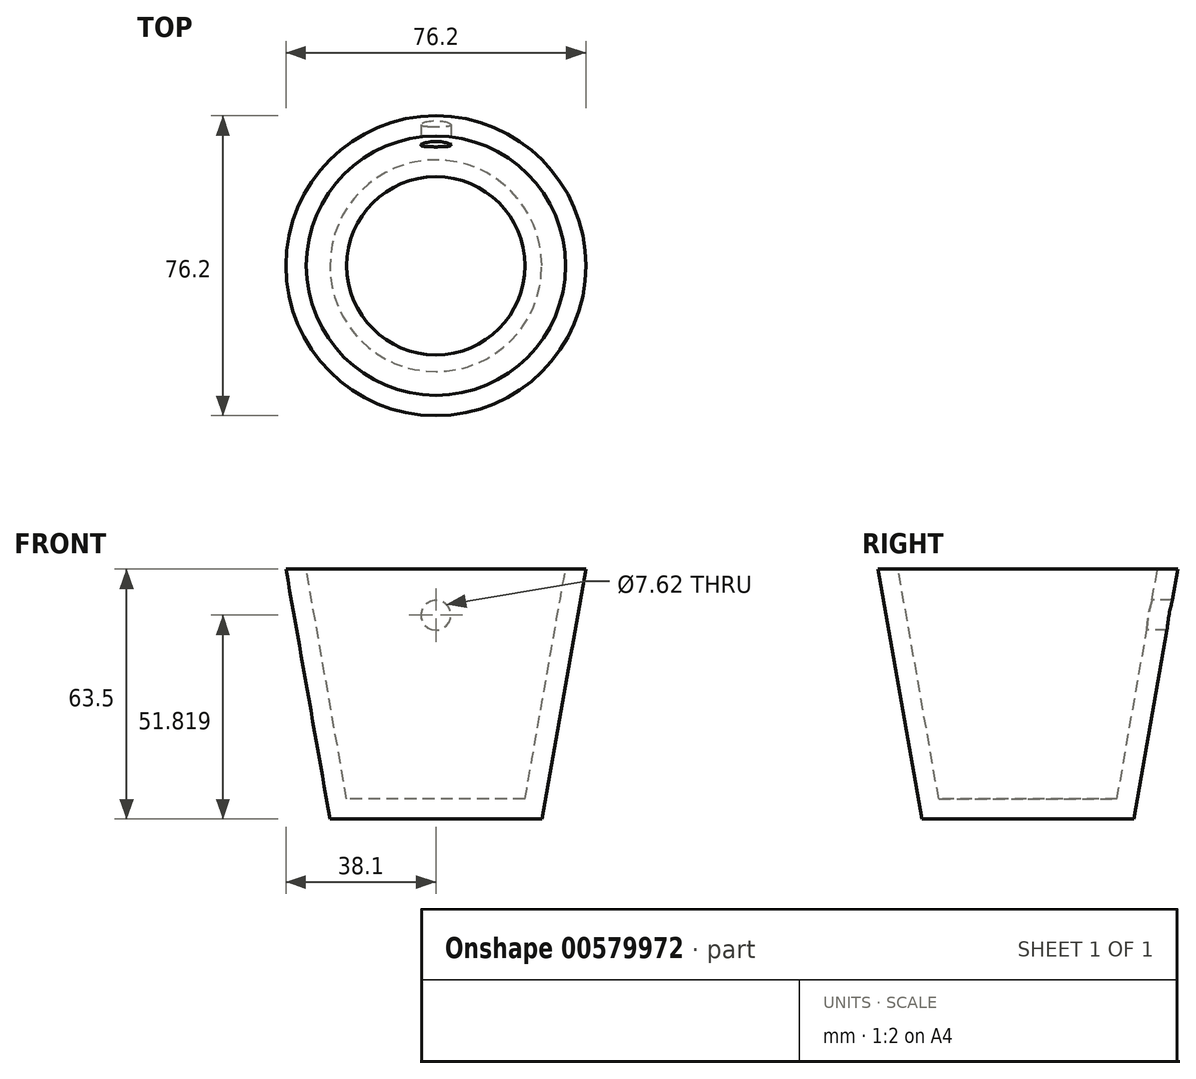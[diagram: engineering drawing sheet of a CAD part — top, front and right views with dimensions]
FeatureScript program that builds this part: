
annotation { "Feature Type Name" : "Feature", "Feature Type Description" : "" }
export const myFeature = defineFeature(function(context is Context, id is Id, definition is map)
    precondition{}
    {
        {
            var Q0;
            Q0=qCreatedBy(makeId("Front.planeOp"),FACE);
            var sketch = newSketch(context, id + "F0", { "sketchPlane" : qUnion([Q0])});
            skLineSegment(sketch, "E0", {"start": v(0, 63.5) * mm, "end": v(-38.1, 63.5) * mm});
            skLineSegment(sketch, "E1", {"start": v(-38.1, 63.5) * mm, "end": v(-26.9, 0) * mm});
            skLineSegment(sketch, "E2", {"start": v(-26.9, 0) * mm, "end": v(0, 0) * mm});
            skLineSegment(sketch, "E3", {"start": v(0, 0) * mm, "end": v(0, 63.5) * mm});
            skSolve(sketch);
        }
        {
            var Q0;
            Q0=makeQuery(id+"F0.imprint","IMPRINT",FACE,{"disambiguationData":[TD([[makeQuery(id+"F0.imprint","IMPRINT",EDGE,{"derivedFrom":sQuery(id+"F0.wireOp",EDGE,"E0")}),1.0]])]});
            var Q1;
            Q1=sQuery(id+"F0.wireOp",EDGE,"E3");
            revolve(context, id + "F1", {"entities" : qUnion([Q0]), "axis" : qUnion([Q1]), "revolveType" : RevolveType.FULL});
        }
        {
            var Q0;
            Q0=makeQuery(id+"F1.opRevolve","SWEPT_FACE",FACE,{"disambiguationData":[OSD([sQuery(id+"F0.wireOp",EDGE,"E0")])]});
            shell(context, id + "F2", {"entities" : qUnion([Q0]), "thickness" : 5.08 * mm});
        }
        {
            var Q0;
            Q0=qCreatedBy(makeId("Front.planeOp"),FACE);
            var sketch = newSketch(context, id + "F3", { "sketchPlane" : qUnion([Q0])});
            skCircle(sketch, "E4", {"center": v(0, 51.82) * mm, "radius": 3.81 * mm});
            skSolve(sketch);
        }
        {
            var Q0;
            Q0=makeQuery(id+"F3.imprint","IMPRINT",FACE,{"disambiguationData":[TD([[makeQuery(id+"F3.imprint","IMPRINT",EDGE,{"derivedFrom":sQuery(id+"F3.wireOp",EDGE,"E4")}),1.0]])]});
            var Q1;
            Q1 = qSketchRegion(id + "F5", true);
            var Q2;
            Q2=sQuery(id+"F3.wireOp",EDGE,"E4");
            extrude(context, id + "F4", {"entities" : qUnion([Q0, Q1]), "operationType" : NewBodyOperationType.REMOVE, "surfaceEntities" : qUnion([Q2]), "oppositeDirection" : true, "depth" : 304.8 * mm, "offsetDistance" : 25.4 * mm});
        }
    });
